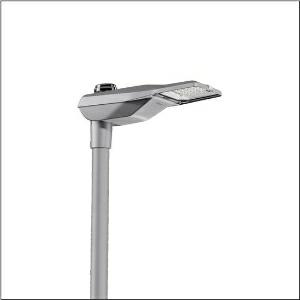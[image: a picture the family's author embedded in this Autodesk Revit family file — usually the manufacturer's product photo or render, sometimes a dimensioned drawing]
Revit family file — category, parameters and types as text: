
# Revit family: streetlight_sl_21_micro___st1_0a_5xe5d47n08db_8e26
name_source: partatom
category: Lighting Fixtures
units: mm (PartAtom-declared; Revit-internal decimal feet)

## family parameters
Cut with Voids When Loaded = No
Host = Face
Light Source = No
Part Type = Normal
Room Calculation Point = No
Round Connector Dimension = Use Diameter
Shared = No

## types (1)
- --- (1 x LED, 5320 lm, 39.1 W, 4000K)
    Apparent Load = 39 VA
    CIE Flux Codes = 37 72 97 100 100
    Color Rendering = 70
    Color Temperature = 4000K
    Default Elevation = 1800 mm
    Description = Streetlight SL 21 micro, mast luminaire, primary light control with lens, of PMMA, primary optical cover: cover, of toughened safety glass, transparent, light distribution: ST1.0a, light emission: direct distribution, primary light characteristic: asymmetric, installation type: post-top, LED, 3G 1.5mm², High Power LED, rated luminous flux: 5.320lm, luminous efficacy: 136lm/W, light colour: 740, colour temperature: 4000K, control gear: NEMA (7pin), control: overheat protection, pre-setting: linear dimming characteristic, constant luminous flux control, time-dependent luminous flux control, flexible luminous flux parameterisation, mains connection: 230..240V, AC, 50/60Hz, connection cable pre-assembled, cable length: 6,5m, wiring characteristics: H07RN-F, start of lifetime: 39W, end of service life: 41W, reduction: 18W, luminaire housing, of diecast aluminium (EN AC-44300), powder-coated, SITECO metallic grey (DB 702S), corrosivity category C5 high according to DIN EN ISO 12944, multi-level sealing system, sealing non-destructively replaceable, inclination adjustable: 0°, 5°, 10°, 15°, length: 528mm, width: 235mm, height: 110mm, spigot size: 76/60mm (post-top), mounting height: 4..8m, protection rating (complete): IP66, insulation class (complete): insulation class I (protective earthing), certification: CE, ENEC, ENEC+, VDE, impact resistance: IK10, permissible operating ambient temperature for outdoor applications: -40..+50°C, standard-compliant lighting for roads and squares, packaging unit: 1 piece

Light Distribution: ST1.0a
    Height = 110 mm
    Lamp = 1 x LED
    Lamp Light Flux = 5320 lm
    Lamp Power = 39.1 W
    Lamp count = 1
    Length = 528 mm
    Luminous efficacy = 136 lm/W
    Manufacturer = Siteco
    ModVariant = No
    Model = 5XE5D47N08DB
    Number of Poles = 1
    OnlyDefault = Yes
    Power Factor = 1
    Product Name = Streetlight SL 21 micro | ST1.0a
    Product group = mast luminaire | pylon top
    ProductGroupID = 6100
    Protection Class = Protection class I
    Protection Degree = IP 66
    RLX_Detail_Level = 1
    RLX_Emergency_Light_Flux = 0 lm
    RLX_Emergency_Type = 0
    RLX_Emergency_Type_DB = No
    RlxData = <blob elided: 98921 chars, md5=e566f546>
    Socket = socket
    Standby Power = 0 W
    System Light Flux = 5320 lm
    System Power = 39 W
    Type Comments = factory setting: luminous flux: 100 % | dim-lin: 254 | 765 mA
    Type Image = l_1294375.jpg
    URL = http://relux.com
    VarID = @adj_135971
    Voltage = 0 V
    Weight = 0.00 kg
    Width = 235 mm

## geometry (parser evidence)
native form markers: Blend x4, Sweep x12
no freeform markers — native parametric forms only
